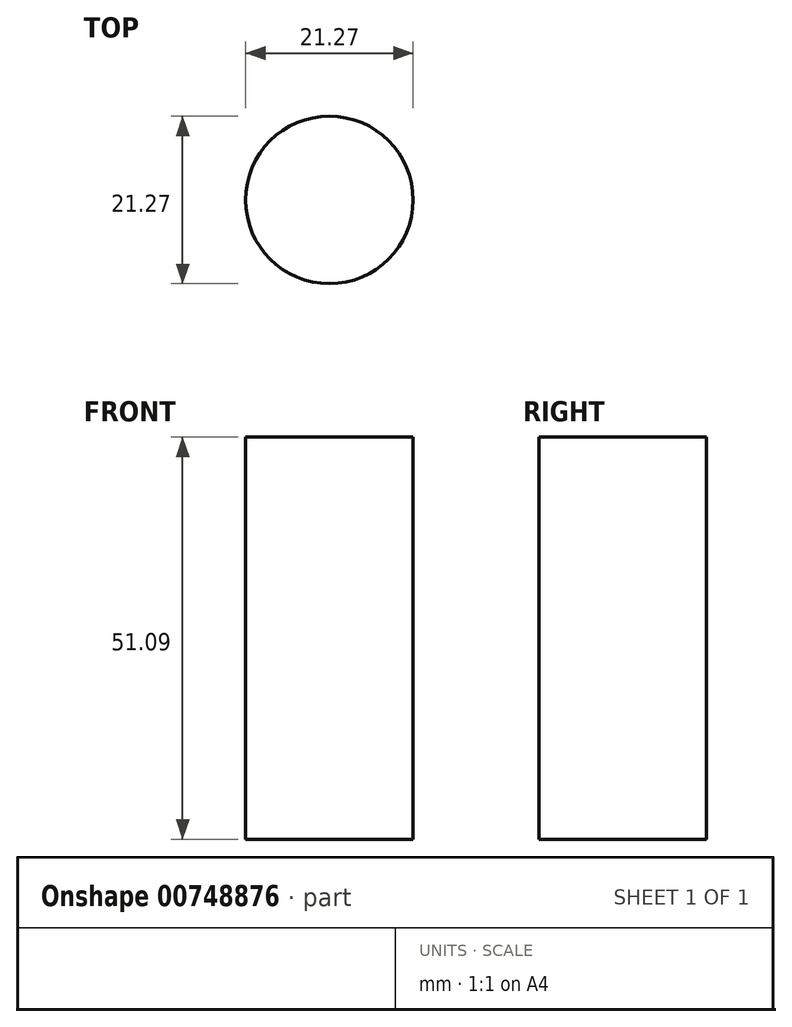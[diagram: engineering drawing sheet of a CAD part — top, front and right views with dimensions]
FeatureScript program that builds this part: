
annotation { "Feature Type Name" : "Feature", "Feature Type Description" : "" }
export const myFeature = defineFeature(function(context is Context, id is Id, definition is map)
    precondition{}
    {
        {
            var Q0;
            Q0=qCreatedBy(makeId("Top.planeOp"),FACE);
            var sketch = newSketch(context, id + "F0", { "sketchPlane" : qUnion([Q0])});
            skCircle(sketch, "E0", {"center": v(-44.17, 45.18) * mm, "radius": 10.63 * mm});
            skSolve(sketch);
        }
        {
            var Q0;
            Q0=sQuery(id+"F0.wireOp",EDGE,"E0");
            extrude(context, id + "F1", {"bodyType" : ToolBodyType.SURFACE, "surfaceEntities" : qUnion([Q0]), "depth" : 51.1 * mm, "offsetDistance" : 25.4 * mm});
        }
    });
